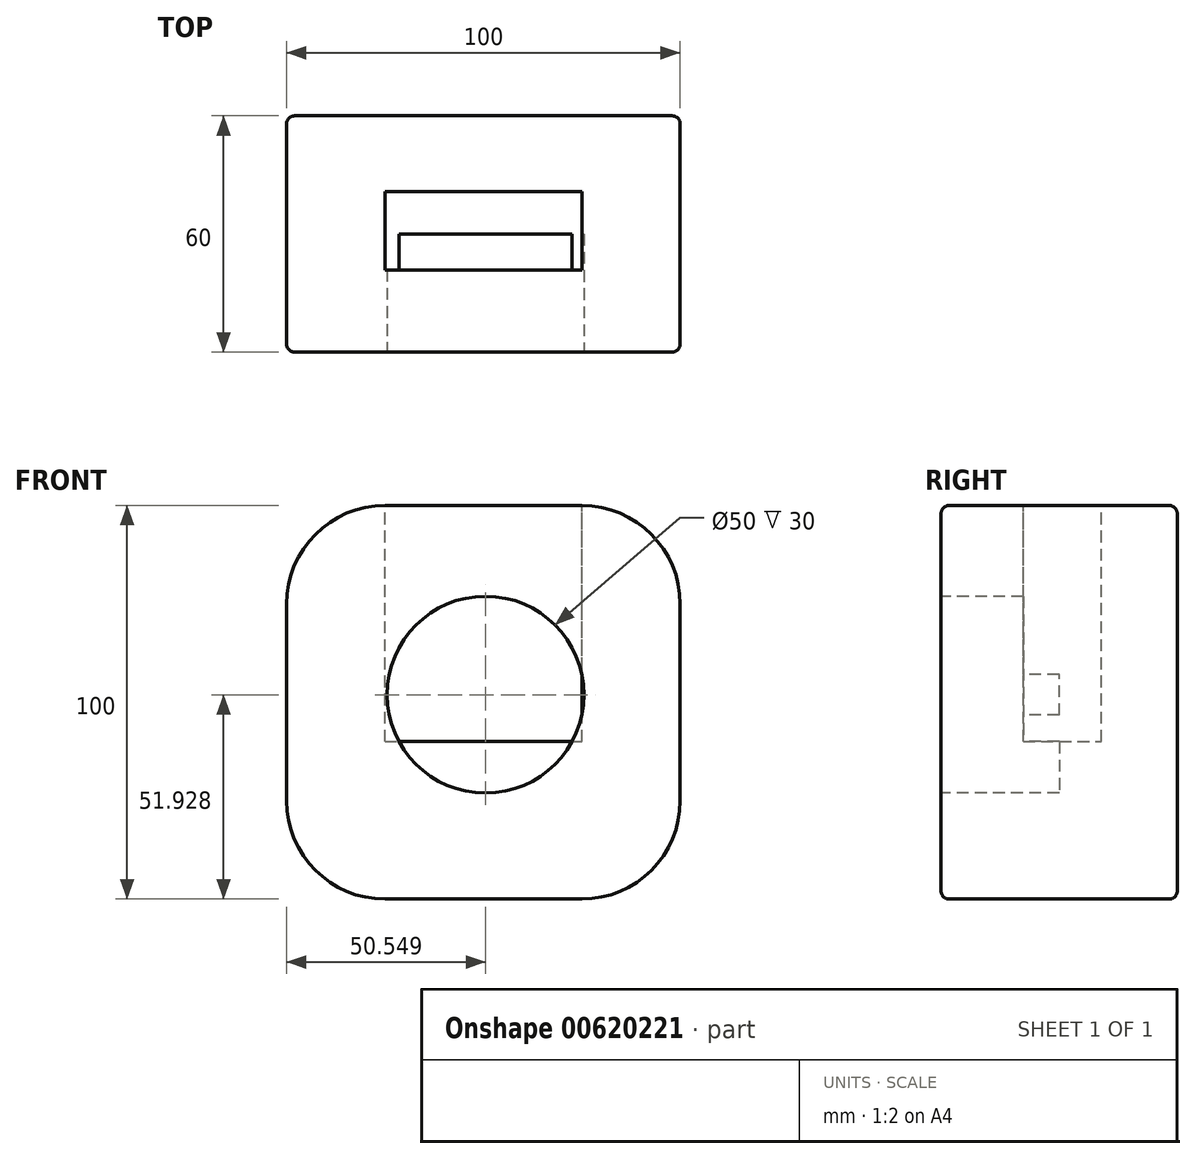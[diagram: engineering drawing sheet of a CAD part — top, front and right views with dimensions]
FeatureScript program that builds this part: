
annotation { "Feature Type Name" : "Feature", "Feature Type Description" : "" }
export const myFeature = defineFeature(function(context is Context, id is Id, definition is map)
    precondition{}
    {
        {
            var Q0;
            Q0=qCreatedBy(makeId("Front.planeOp"),FACE);
            var sketch = newSketch(context, id + "F0", { "sketchPlane" : qUnion([Q0])});
            skLineSegment(sketch, "E0.bottom", {"start": v(-22.1, 68.59) * mm, "end": v(27.9, 68.59) * mm});
            skLineSegment(sketch, "E0.top", {"start": v(-22.1, -31.41) * mm, "end": v(27.9, -31.41) * mm});
            skLineSegment(sketch, "E0.left", {"start": v(-47.1, 43.59) * mm, "end": v(-47.1, -6.41) * mm});
            skLineSegment(sketch, "E0.right", {"start": v(52.9, 43.59) * mm, "end": v(52.9, -6.41) * mm});
            skPoint(sketch, "E1.visualSharp", {"position": v(-47.1, 68.59) * mm});
            skArc(sketch, "E1.filletArc", {"start": v(-22.1, 68.59) * mm, "mid": v(-39.79, 61.26) * mm, "end": v(-47.1, 43.59) * mm});
            skPoint(sketch, "E2.visualSharp", {"position": v(-47.1, -31.41) * mm});
            skArc(sketch, "E2.filletArc", {"start": v(-47.1, -6.41) * mm, "mid": v(-39.79, -24.1) * mm, "end": v(-22.1, -31.41) * mm});
            skPoint(sketch, "E3.visualSharp", {"position": v(52.9, -31.41) * mm});
            skArc(sketch, "E3.filletArc", {"start": v(27.9, -31.41) * mm, "mid": v(45.57, -24.1) * mm, "end": v(52.9, -6.41) * mm});
            skPoint(sketch, "E4.visualSharp", {"position": v(52.9, 68.59) * mm});
            skArc(sketch, "E4.filletArc", {"start": v(52.9, 43.59) * mm, "mid": v(45.57, 61.26) * mm, "end": v(27.9, 68.59) * mm});
            skSolve(sketch);
        }
        {
            var Q0;
            Q0=makeQuery(id+"F0.imprint","IMPRINT",FACE,{"disambiguationData":[TD([[makeQuery(id+"F0.imprint","IMPRINT",EDGE,{"derivedFrom":sQuery(id+"F0.wireOp",EDGE,"E0.bottom")}),-1.0]])]});
            extrude(context, id + "F1", {"entities" : qUnion([Q0]), "endBound" : BoundingType.SYMMETRIC, "depth" : 60 * mm, "offsetDistance" : 25 * mm});
        }
        {
            var Q0;
            Q0=makeQuery(id+"F1.opExtrude","CAP_FACE",FACE,{"disambiguationData":[OSD([sQuery(id+"F0.wireOp",EDGE,"E0.bottom"),sQuery(id+"F0.wireOp",EDGE,"E0.top"),sQuery(id+"F0.wireOp",EDGE,"E0.left"),sQuery(id+"F0.wireOp",EDGE,"E0.right"),sQuery(id+"F0.wireOp",EDGE,"E1.filletArc"),sQuery(id+"F0.wireOp",EDGE,"E2.filletArc"),sQuery(id+"F0.wireOp",EDGE,"E3.filletArc"),sQuery(id+"F0.wireOp",EDGE,"E4.filletArc")])],"isStart":true});
            fillet(context, id + "F2", {"entities" : qUnion([Q0]), "radius" : 2 * mm, "tangentPropagation" : true, "allowEdgeOverflow" : false});
        }
        {
            var Q0;
            Q0=makeQuery(id+"F1.opExtrude","CAP_FACE",FACE,{"disambiguationData":[OSD([sQuery(id+"F0.wireOp",EDGE,"E0.bottom"),sQuery(id+"F0.wireOp",EDGE,"E0.top"),sQuery(id+"F0.wireOp",EDGE,"E0.left"),sQuery(id+"F0.wireOp",EDGE,"E0.right"),sQuery(id+"F0.wireOp",EDGE,"E1.filletArc"),sQuery(id+"F0.wireOp",EDGE,"E2.filletArc"),sQuery(id+"F0.wireOp",EDGE,"E3.filletArc"),sQuery(id+"F0.wireOp",EDGE,"E4.filletArc")])],"isStart":false});
            fillet(context, id + "F3", {"entities" : qUnion([Q0]), "radius" : 2 * mm, "tangentPropagation" : true, "allowEdgeOverflow" : false});
        }
        {
            var Q0;
            Q0=makeQuery(id+"F1.opExtrude","CAP_FACE",FACE,{"disambiguationData":[OSD([sQuery(id+"F0.wireOp",EDGE,"E0.bottom"),sQuery(id+"F0.wireOp",EDGE,"E0.top"),sQuery(id+"F0.wireOp",EDGE,"E0.left"),sQuery(id+"F0.wireOp",EDGE,"E0.right"),sQuery(id+"F0.wireOp",EDGE,"E1.filletArc"),sQuery(id+"F0.wireOp",EDGE,"E2.filletArc"),sQuery(id+"F0.wireOp",EDGE,"E3.filletArc"),sQuery(id+"F0.wireOp",EDGE,"E4.filletArc")])],"isStart":false});
            var sketch = newSketch(context, id + "F4", { "sketchPlane" : qUnion([Q0])});
            skCircle(sketch, "E5", {"center": v(3.44, 20.52) * mm, "radius": 25 * mm});
            skSolve(sketch);
        }
        {
            var Q0;
            Q0 = qSketchRegion(id + "F4", true);
            extrude(context, id + "F5", {"entities" : qUnion([Q0]), "operationType" : NewBodyOperationType.REMOVE, "oppositeDirection" : true, "depth" : 30 * mm, "offsetDistance" : 25 * mm});
        }
        {
            var Q0;
            Q0=makeQuery(id+"F1.opExtrude","SWEPT_FACE",FACE,{"disambiguationData":[OSD([sQuery(id+"F0.wireOp",EDGE,"E0.bottom")])]});
            var sketch = newSketch(context, id + "F6", { "sketchPlane" : qUnion([Q0])});
            skLineSegment(sketch, "E6.bottom", {"start": v(-22.1, 10.8) * mm, "end": v(27.9, 10.8) * mm});
            skLineSegment(sketch, "E6.top", {"start": v(-22.1, -9.13) * mm, "end": v(27.9, -9.13) * mm});
            skLineSegment(sketch, "E6.left", {"start": v(-22.1, 10.8) * mm, "end": v(-22.1, -9.13) * mm});
            skLineSegment(sketch, "E6.right", {"start": v(27.9, 10.8) * mm, "end": v(27.9, -9.13) * mm});
            skSolve(sketch);
        }
        {
            var Q0;
            Q0=makeQuery(id+"F6.imprint","IMPRINT",FACE,{"disambiguationData":[TD([[makeQuery(id+"F6.imprint","IMPRINT",EDGE,{"derivedFrom":sQuery(id+"F6.wireOp",EDGE,"E6.bottom")}),-1.0]])]});
            extrude(context, id + "F7", {"entities" : qUnion([Q0]), "operationType" : NewBodyOperationType.REMOVE, "oppositeDirection" : true, "depth" : 60 * mm, "offsetDistance" : 25 * mm});
        }
    });
